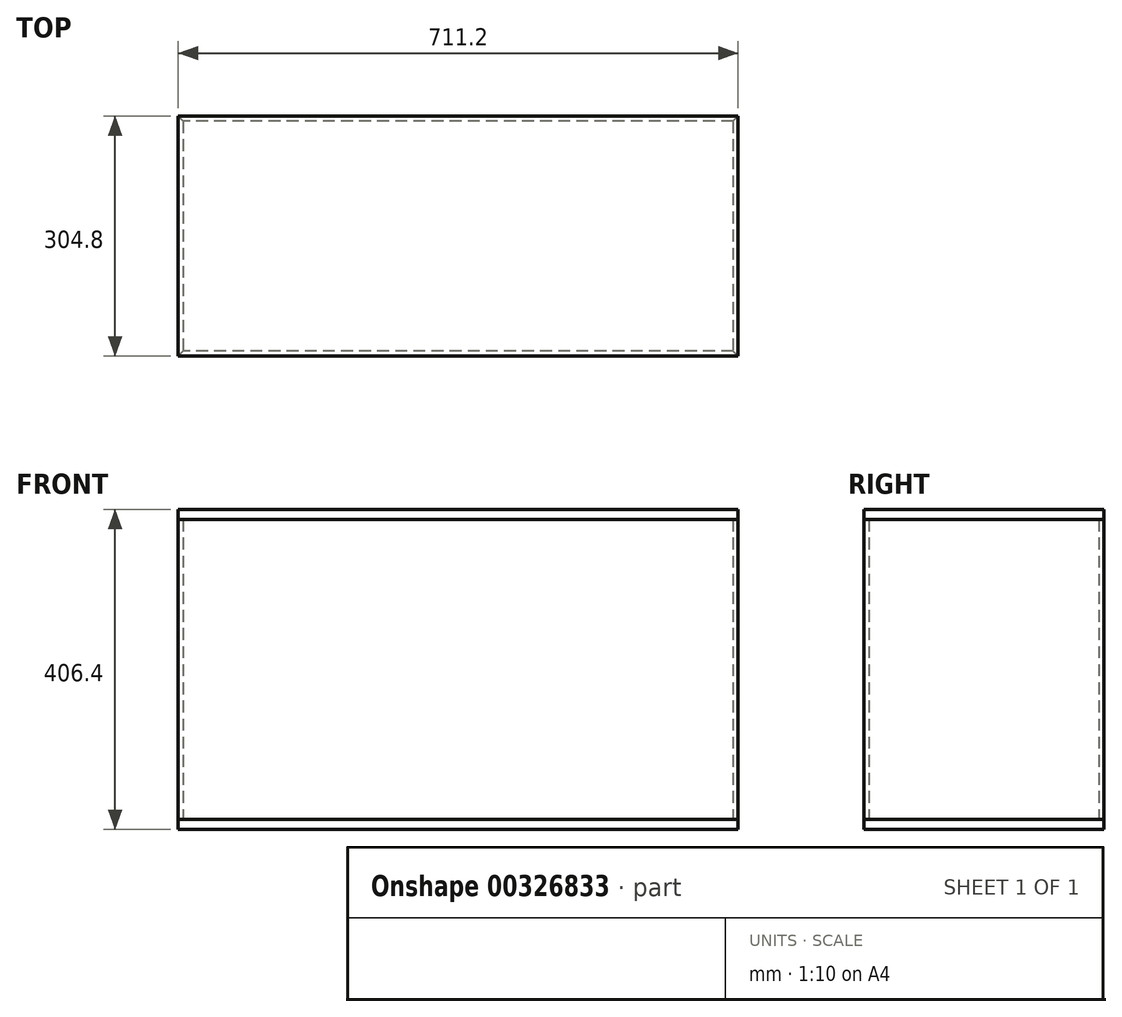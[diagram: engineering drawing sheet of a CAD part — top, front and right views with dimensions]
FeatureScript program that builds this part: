
annotation { "Feature Type Name" : "Feature", "Feature Type Description" : "" }
export const myFeature = defineFeature(function(context is Context, id is Id, definition is map)
    precondition{}
    {
        {
            var Q0;
            Q0=qCreatedBy(makeId("Top.planeOp"),FACE);
            cPlane(context, id + "F0", {"entities" : qUnion([Q0]), "cplaneType" : CPlaneType.OFFSET, "offset" : 406.4 * mm, "width" : 152.4 * mm, "height" : 152.4 * mm});
        }
        {
            var Q0;
            Q0=qCreatedBy(makeId("Top.planeOp"),FACE);
            var sketch = newSketch(context, id + "F1", { "sketchPlane" : qUnion([Q0])});
            skLineSegment(sketch, "E0.bottom", {"start": v(0, 0) * mm, "end": v(711.2, 0) * mm});
            skLineSegment(sketch, "E0.top", {"start": v(0, 304.8) * mm, "end": v(711.2, 304.8) * mm});
            skLineSegment(sketch, "E0.left", {"start": v(0, 0) * mm, "end": v(0, 304.8) * mm});
            skLineSegment(sketch, "E0.right", {"start": v(711.2, 0) * mm, "end": v(711.2, 304.8) * mm});
            skSolve(sketch);
        }
        {
            var Q0;
            Q0=makeQuery(id+"F1.imprint","IMPRINT",FACE,{"disambiguationData":[TD([[makeQuery(id+"F1.imprint","IMPRINT",EDGE,{"derivedFrom":sQuery(id+"F1.wireOp",EDGE,"E0.bottom")}),1.0]])]});
            extrude(context, id + "F2", {"entities" : qUnion([Q0]), "depth" : 12.7 * mm});
        }
        {
            var Q0;
            Q0=qCreatedBy(id+"F0.planeOp",FACE);
            var sketch = newSketch(context, id + "F3", { "sketchPlane" : qUnion([Q0])});
            skLineSegment(sketch, "E1.bottom", {"start": v(0, 0) * mm, "end": v(711.2, 0) * mm});
            skLineSegment(sketch, "E1.top", {"start": v(0, 304.8) * mm, "end": v(711.2, 304.8) * mm});
            skLineSegment(sketch, "E1.left", {"start": v(0, 0) * mm, "end": v(0, 304.8) * mm});
            skLineSegment(sketch, "E1.right", {"start": v(711.2, 0) * mm, "end": v(711.2, 304.8) * mm});
            skSolve(sketch);
        }
        {
            var Q0;
            Q0 = qSketchRegion(id + "F3", true);
            extrude(context, id + "F4", {"entities" : qUnion([Q0]), "oppositeDirection" : true, "depth" : 12.7 * mm});
        }
        {
            var Q0;
            Q0=makeQuery(id+"F2.opExtrude","CAP_FACE",FACE,{"disambiguationData":[OSD([sQuery(id+"F1.wireOp",EDGE,"E0.bottom"),sQuery(id+"F1.wireOp",EDGE,"E0.top"),sQuery(id+"F1.wireOp",EDGE,"E0.left"),sQuery(id+"F1.wireOp",EDGE,"E0.right")])],"isStart":false});
            var sketch = newSketch(context, id + "F5", { "sketchPlane" : qUnion([Q0])});
            skLineSegment(sketch, "E2", {"start": v(0, 304.8) * mm, "end": v(711.2, 304.8) * mm});
            skLineSegment(sketch, "E3", {"start": v(711.2, 304.8) * mm, "end": v(704.85, 298.45) * mm});
            skLineSegment(sketch, "E4", {"start": v(704.85, 298.45) * mm, "end": v(6.35, 298.45) * mm});
            skLineSegment(sketch, "E5", {"start": v(6.35, 298.45) * mm, "end": v(0, 304.8) * mm});
            skSolve(sketch);
        }
        {
            var Q0;
            Q0 = qSketchRegion(id + "F5", true);
            var Q1;
            Q1=makeQuery(id+"F4.opExtrude","CAP_FACE",FACE,{"disambiguationData":[OSD([sQuery(id+"F3.wireOp",EDGE,"E1.bottom"),sQuery(id+"F3.wireOp",EDGE,"E1.top"),sQuery(id+"F3.wireOp",EDGE,"E1.left"),sQuery(id+"F3.wireOp",EDGE,"E1.right")])],"isStart":false});
            extrude(context, id + "F6", {"entities" : qUnion([Q0]), "endBound" : BoundingType.UP_TO_SURFACE, "endBoundEntityFace" : qUnion([Q1]), "depth" : 25.4 * mm});
        }
        {
            var Q0;
            Q0=makeQuery(id+"F2.opExtrude","CAP_FACE",FACE,{"disambiguationData":[OSD([sQuery(id+"F1.wireOp",EDGE,"E0.bottom"),sQuery(id+"F1.wireOp",EDGE,"E0.top"),sQuery(id+"F1.wireOp",EDGE,"E0.left"),sQuery(id+"F1.wireOp",EDGE,"E0.right")])],"isStart":false});
            var sketch = newSketch(context, id + "F7", { "sketchPlane" : qUnion([Q0])});
            skLineSegment(sketch, "E6", {"start": v(0, 304.8) * mm, "end": v(6.35, 298.45) * mm});
            skLineSegment(sketch, "E7", {"start": v(6.35, 298.45) * mm, "end": v(6.35, 6.35) * mm});
            skLineSegment(sketch, "E8", {"start": v(6.35, 6.35) * mm, "end": v(0, 0) * mm});
            skLineSegment(sketch, "E9", {"start": v(0, 0) * mm, "end": v(0, 304.8) * mm});
            skSolve(sketch);
        }
        {
            var Q0;
            Q0 = qSketchRegion(id + "F7", true);
            var Q1;
            Q1=makeQuery(id+"F4.opExtrude","CAP_FACE",FACE,{"disambiguationData":[OSD([sQuery(id+"F3.wireOp",EDGE,"E1.bottom"),sQuery(id+"F3.wireOp",EDGE,"E1.top"),sQuery(id+"F3.wireOp",EDGE,"E1.left"),sQuery(id+"F3.wireOp",EDGE,"E1.right")])],"isStart":false});
            extrude(context, id + "F8", {"entities" : qUnion([Q0]), "endBound" : BoundingType.UP_TO_SURFACE, "endBoundEntityFace" : qUnion([Q1]), "depth" : 25.4 * mm});
        }
        {
            var Q0;
            Q0=makeQuery(id+"F2.opExtrude","SWEPT_FACE",FACE,{"disambiguationData":[OSD([sQuery(id+"F1.wireOp",EDGE,"E0.right")])]});
            var Q1;
            Q1=makeQuery(id+"F2.opExtrude","SWEPT_FACE",FACE,{"disambiguationData":[OSD([sQuery(id+"F1.wireOp",EDGE,"E0.left")])]});
            cPlane(context, id + "F9", {"entities" : qUnion([Q0, Q1]), "cplaneType" : CPlaneType.MID_PLANE, "offset" : 25.4 * mm, "width" : 152.4 * mm, "height" : 152.4 * mm});
        }
        {
            var Q0;
            Q0=makeQuery(id+"F2.opExtrude","SWEPT_FACE",FACE,{"disambiguationData":[OSD([sQuery(id+"F1.wireOp",EDGE,"E0.bottom")])]});
            var Q1;
            Q1=makeQuery(id+"F2.opExtrude","SWEPT_FACE",FACE,{"disambiguationData":[OSD([sQuery(id+"F1.wireOp",EDGE,"E0.top")])]});
            cPlane(context, id + "F10", {"entities" : qUnion([Q0, Q1]), "cplaneType" : CPlaneType.MID_PLANE, "offset" : 25.4 * mm, "width" : 152.4 * mm, "height" : 152.4 * mm});
        }
        {
            var Q0;
            Q0=makeQuery(id+"F8.opExtrude","SWEPT_BODY",BODY,{"disambiguationData":[OSD([sQuery(id+"F7.wireOp",EDGE,"E6"),sQuery(id+"F7.wireOp",EDGE,"E7"),sQuery(id+"F7.wireOp",EDGE,"E8"),sQuery(id+"F7.wireOp",EDGE,"E9")])]});
            var Q1;
            Q1=qCreatedBy(id+"F9.planeOp",FACE);
            mirror(context, id + "F11", {"entities" : qUnion([Q0]), "mirrorPlane" : qUnion([Q1])});
        }
        {
            var Q0;
            Q0=makeQuery(id+"F6.opExtrude","SWEPT_BODY",BODY,{"disambiguationData":[OSD([sQuery(id+"F5.wireOp",EDGE,"E2"),sQuery(id+"F5.wireOp",EDGE,"E3"),sQuery(id+"F5.wireOp",EDGE,"E4"),sQuery(id+"F5.wireOp",EDGE,"E5")])]});
            var Q1;
            Q1=qCreatedBy(id+"F10.planeOp",FACE);
            mirror(context, id + "F12", {"entities" : qUnion([Q0]), "mirrorPlane" : qUnion([Q1])});
        }
    });
